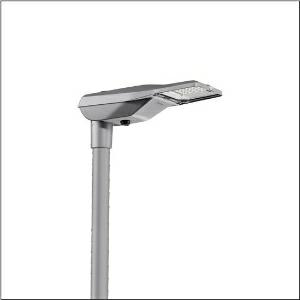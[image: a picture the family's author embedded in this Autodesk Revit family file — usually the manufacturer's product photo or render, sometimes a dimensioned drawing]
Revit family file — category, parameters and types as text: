
# Revit family: streetlight_sl_21_micro___p0_8a_5xe1u33r08db_bf72
name_source: partatom
category: Lighting Fixtures
units: mm (PartAtom-declared; Revit-internal decimal feet)

## family parameters
Cut with Voids When Loaded = No
Host = Face
Light Source = No
Part Type = Normal
Room Calculation Point = No
Round Connector Dimension = Use Diameter
Shared = No

## types (1)
- --- (1 x LED, 5040 lm, 39.1 W, 3000K)
    Apparent Load = 39 VA
    CIE Flux Codes = 33 69 96 100 100
    Color Rendering = 70
    Color Temperature = 3000K
    Default Elevation = 1800 mm
    Description = Streetlight SL 21 micro, mast luminaire, primary light control with lens, of PMMA, primary optical cover: cover, of toughened safety glass, transparent, light distribution: P0.8a, light emission: direct distribution, primary light characteristic: asymmetric, installation type: post-top, side-entry, LED, High Power LED, rated luminous flux: 5.040lm, luminous efficacy: 129lm/W, light colour: 730, colour temperature: 3000K, control gear: D4i, control: pre-setting: logarithmic dimming characteristic, flexible luminous flux parameterisation, time-dependent luminous flux control, constant luminous flux control, overheat protection, mains connection: 220..240V, AC, 50/60Hz, start of lifetime: 39W, end of service life: 41W, reduction: 18W, luminaire housing, of diecast aluminium, powder-coated, Siteco® metallic grey (DB 702S), corrosivity category C5 mid according to DIN EN ISO 12944, multi-level sealing system, sealing non-destructively replaceable, inclination adjustable: 0°, 5°, 10°, 15°, please order mast flange separately, length: 528mm, width: 235mm, height: 110mm, mast flange for spigot size: 42mm (side-entry): 5XC10008XM4, 60/48mm (side-entry/post-top): 5XC10108XM2, 76/60mm (side-entry/post-top): 5XC10108XM1, Smart Interface below, protection rating (complete): IP66, insulation class (complete): insulation class II (safety insulation), certification: CE, ENEC, ENEC+, VDE, impact resistance: IK10, permissible operating ambient temperature for outdoor applications: -40..+50°C, standard-compliant lighting for roads and squares, packaging unit: 1 piece

Light Distribution: P0.8a
    Height = 110 mm
    Lamp = 1 x LED
    Lamp Light Flux = 5040 lm
    Lamp Power = 39.1 W
    Lamp count = 1
    Length = 528 mm
    Luminous efficacy = 129 lm/W
    Manufacturer = Siteco
    ModVariant = No
    Model = 5XE1U33R08DB
    Number of Poles = 1
    OnlyDefault = Yes
    Power Factor = 1
    Product Name = Streetlight SL 21 micro | P0.8a
    Product group = mast luminaire | pylon top
    ProductGroupID = 6100
    Protection Class = Protection class II
    Protection Degree = IP 66
    RLX_Detail_Level = 1
    RLX_Emergency_Light_Flux = 0 lm
    RLX_Emergency_Type = 0
    RLX_Emergency_Type_DB = No
    RlxData = <blob elided: 99193 chars, md5=ab5d5c4e>
    Socket = socket
    Standby Power = 0 W
    System Light Flux = 5040 lm
    System Power = 39 W
    Type Comments = factory setting: luminous flux: 100 % | dim-lin: 254 | 765 mA
    Type Image = l_1277290.jpg
    URL = http://relux.com
    VarID = @adj_094375
    Voltage = 0 V
    Weight = 0.00 kg
    Width = 235 mm

## geometry (parser evidence)
native form markers: Blend x4, Sweep x10
no freeform markers — native parametric forms only
